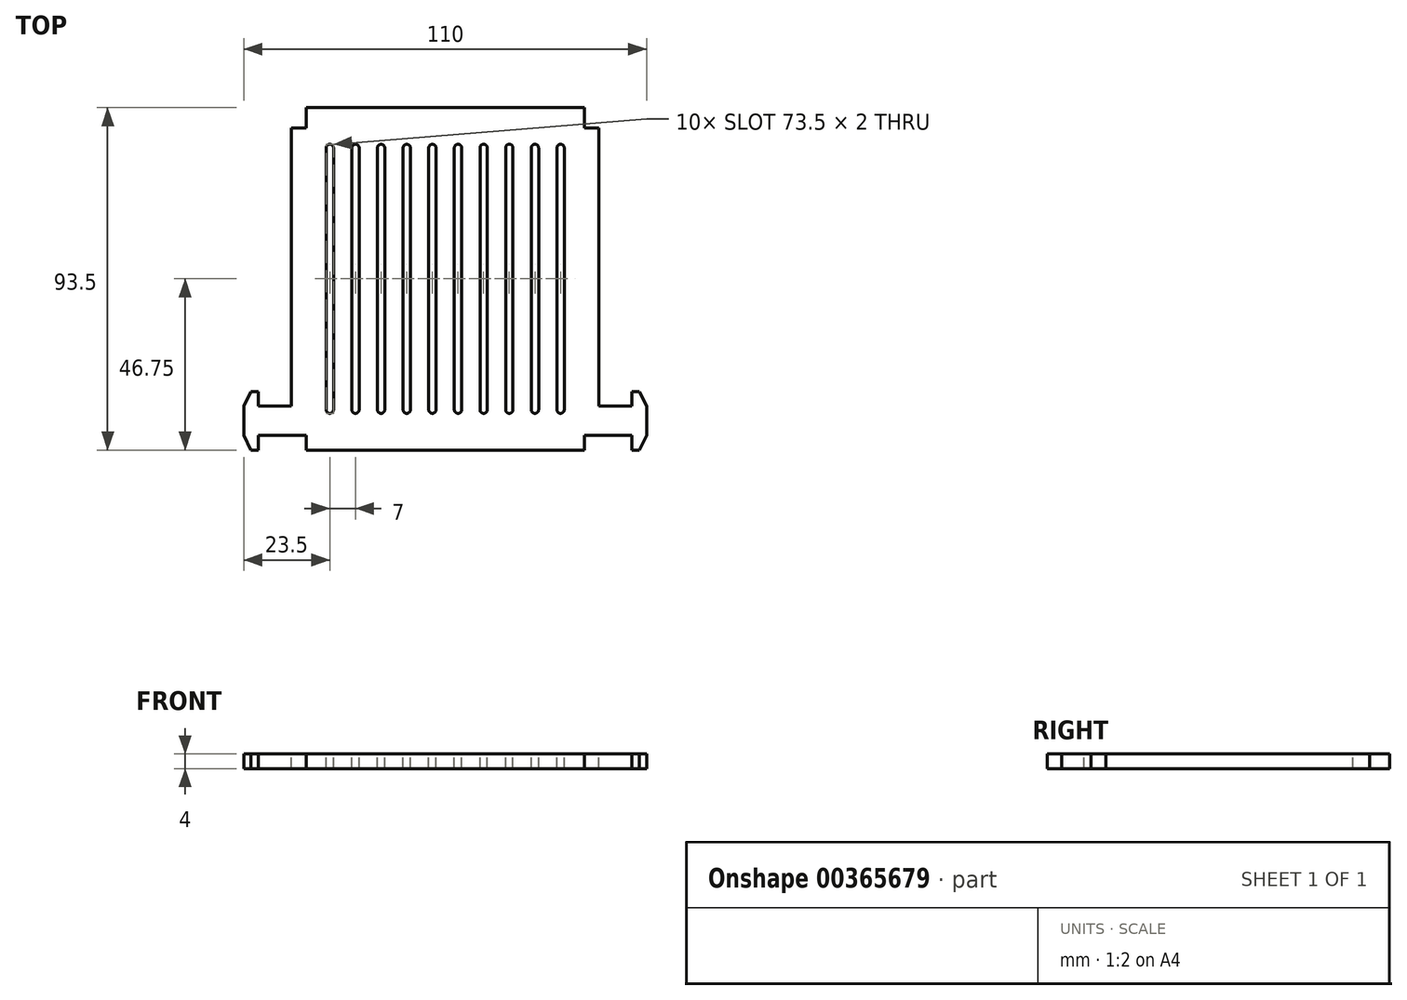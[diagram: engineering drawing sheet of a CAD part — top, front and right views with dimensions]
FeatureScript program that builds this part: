
annotation { "Feature Type Name" : "Feature", "Feature Type Description" : "" }
export const myFeature = defineFeature(function(context is Context, id is Id, definition is map)
    precondition{}
    {
        {
            var Q0;
            Q0=qCreatedBy(makeId("Top.planeOp"),FACE);
            var sketch = newSketch(context, id + "F0", { "sketchPlane" : qUnion([Q0])});
            skLineSegment(sketch, "E0.bottom", {"start": v(0, 0) * mm, "end": v(84, 0) * mm});
            skLineSegment(sketch, "E0.top", {"start": v(0, 93.5) * mm, "end": v(84, 93.5) * mm});
            skLineSegment(sketch, "E0.left", {"start": v(0, 0) * mm, "end": v(0, 93.5) * mm});
            skLineSegment(sketch, "E0.right", {"start": v(84, 0) * mm, "end": v(84, 93.5) * mm});
            skSolve(sketch);
        }
        {
            var Q0;
            Q0=qSketchRegion(id+"F0",true);
            extrude(context, id + "F1", {"entities" : qUnion([Q0]), "depth" : 4 * mm});
        }
        {
            var Q0;
            Q0=makeQuery(id+"F1.opExtrude","CAP_FACE",FACE,{"disambiguationData":[OSD([sQuery(id+"F0.wireOp",EDGE,"E0.bottom"),sQuery(id+"F0.wireOp",EDGE,"E0.top"),sQuery(id+"F0.wireOp",EDGE,"E0.left"),sQuery(id+"F0.wireOp",EDGE,"E0.right")])],"isStart":false});
            var sketch = newSketch(context, id + "F2", { "sketchPlane" : qUnion([Q0])});
            skLineSegment(sketch, "E1.bottom", {"start": v(0, 0) * mm, "end": v(4, 0) * mm});
            skLineSegment(sketch, "E1.top", {"start": v(0, 4) * mm, "end": v(4, 4) * mm});
            skLineSegment(sketch, "E1.left", {"start": v(0, 0) * mm, "end": v(0, 4) * mm});
            skLineSegment(sketch, "E1.right", {"start": v(4, 0) * mm, "end": v(4, 4) * mm});
            skLineSegment(sketch, "E2.1.0.0", {"start": v(80, 0) * mm, "end": v(84, 0) * mm});
            skLineSegment(sketch, "E2.1.0.1", {"start": v(80, 4) * mm, "end": v(84, 4) * mm});
            skLineSegment(sketch, "E2.1.0.2", {"start": v(80, 0) * mm, "end": v(80, 4) * mm});
            skLineSegment(sketch, "E2.1.0.3", {"start": v(84, 0) * mm, "end": v(84, 4) * mm});
            skLineSegment(sketch, "E2.direction1", {"start": v(0, 0) * mm, "end": v(80, 0) * mm, "construction": true});
            skLineSegment(sketch, "E2.direction2", {"start": v(0, 0) * mm, "end": v(0, 88) * mm, "construction": true});
            skLineSegment(sketch, "E3", {"start": v(0, 88) * mm, "end": v(84, 88) * mm, "construction": true});
            skLineSegment(sketch, "E4.bottom", {"start": v(0, 88) * mm, "end": v(4, 88) * mm});
            skLineSegment(sketch, "E4.top", {"start": v(0, 93.5) * mm, "end": v(4, 93.5) * mm});
            skLineSegment(sketch, "E4.left", {"start": v(0, 88) * mm, "end": v(0, 93.5) * mm});
            skLineSegment(sketch, "E4.right", {"start": v(4, 88) * mm, "end": v(4, 93.5) * mm});
            skLineSegment(sketch, "E5.bottom", {"start": v(84, 88) * mm, "end": v(80, 88) * mm});
            skLineSegment(sketch, "E5.top", {"start": v(84, 93.5) * mm, "end": v(80, 93.5) * mm});
            skLineSegment(sketch, "E5.left", {"start": v(84, 88) * mm, "end": v(84, 93.5) * mm});
            skLineSegment(sketch, "E5.right", {"start": v(80, 88) * mm, "end": v(80, 93.5) * mm});
            skSolve(sketch);
        }
        {
            var Q0;
            Q0=qSketchRegion(id+"F2",true);
            extrude(context, id + "F3", {"entities" : qUnion([Q0]), "operationType" : NewBodyOperationType.REMOVE, "endBound" : BoundingType.UP_TO_NEXT, "oppositeDirection" : true, "depth" : 25 * mm});
        }
        {
            var Q0;
            Q0=makeQuery(id+"F1.opExtrude","CAP_FACE",FACE,{"disambiguationData":[OSD([sQuery(id+"F0.wireOp",EDGE,"E0.bottom"),sQuery(id+"F0.wireOp",EDGE,"E0.top"),sQuery(id+"F0.wireOp",EDGE,"E0.left"),sQuery(id+"F0.wireOp",EDGE,"E0.right")])],"isStart":false});
            var sketch = newSketch(context, id + "F4", { "sketchPlane" : qUnion([Q0])});
            skLineSegment(sketch, "E6.bottom", {"start": v(10.5, 83.5) * mm, "end": v(10.5, 83.5) * mm});
            skLineSegment(sketch, "E6.top", {"start": v(10.5, 10) * mm, "end": v(10.5, 10) * mm});
            skLineSegment(sketch, "E6.left", {"start": v(9.5, 82.5) * mm, "end": v(9.5, 11) * mm});
            skLineSegment(sketch, "E6.right", {"start": v(11.5, 82.5) * mm, "end": v(11.5, 11) * mm});
            skPoint(sketch, "E7.visualSharp", {"position": v(9.5, 83.5) * mm});
            skArc(sketch, "E7.filletArc", {"start": v(10.5, 83.5) * mm, "mid": v(9.8, 83.2) * mm, "end": v(9.5, 82.5) * mm});
            skArc(sketch, "E8.filletArc", {"start": v(11.5, 82.5) * mm, "mid": v(11.2, 83.2) * mm, "end": v(10.5, 83.5) * mm});
            skPoint(sketch, "E9.visualSharp", {"position": v(11.5, 10) * mm});
            skArc(sketch, "E9.filletArc", {"start": v(10.5, 10) * mm, "mid": v(11.2, 10.3) * mm, "end": v(11.5, 11) * mm});
            skPoint(sketch, "E10.visualSharp", {"position": v(9.5, 10) * mm});
            skArc(sketch, "E10.filletArc", {"start": v(9.5, 11) * mm, "mid": v(9.8, 10.3) * mm, "end": v(10.5, 10) * mm});
            skPoint(sketch, "E11.1.0.0", {"position": v(16.5, 83.5) * mm});
            skLineSegment(sketch, "E11.1.0.1", {"start": v(16.5, 82.5) * mm, "end": v(16.5, 11) * mm});
            skLineSegment(sketch, "E11.1.0.2", {"start": v(18.5, 82.5) * mm, "end": v(18.5, 11) * mm});
            skPoint(sketch, "E11.1.0.3", {"position": v(18.5, 10) * mm});
            skPoint(sketch, "E11.1.0.4", {"position": v(16.5, 10) * mm});
            skArc(sketch, "E11.1.0.5", {"start": v(17.5, 10) * mm, "mid": v(18.2, 10.3) * mm, "end": v(18.5, 11) * mm});
            skArc(sketch, "E11.1.0.6", {"start": v(17.5, 83.5) * mm, "mid": v(16.8, 83.2) * mm, "end": v(16.5, 82.5) * mm});
            skArc(sketch, "E11.1.0.7", {"start": v(16.5, 11) * mm, "mid": v(16.8, 10.3) * mm, "end": v(17.5, 10) * mm});
            skArc(sketch, "E11.1.0.8", {"start": v(18.5, 82.5) * mm, "mid": v(18.2, 83.2) * mm, "end": v(17.5, 83.5) * mm});
            skPoint(sketch, "E11.2.0.0", {"position": v(23.5, 83.5) * mm});
            skLineSegment(sketch, "E11.2.0.1", {"start": v(23.5, 82.5) * mm, "end": v(23.5, 11) * mm});
            skLineSegment(sketch, "E11.2.0.2", {"start": v(25.5, 82.5) * mm, "end": v(25.5, 11) * mm});
            skPoint(sketch, "E11.2.0.3", {"position": v(25.5, 10) * mm});
            skPoint(sketch, "E11.2.0.4", {"position": v(23.5, 10) * mm});
            skArc(sketch, "E11.2.0.5", {"start": v(24.5, 10) * mm, "mid": v(25.2, 10.3) * mm, "end": v(25.5, 11) * mm});
            skArc(sketch, "E11.2.0.6", {"start": v(24.5, 83.5) * mm, "mid": v(23.8, 83.2) * mm, "end": v(23.5, 82.5) * mm});
            skArc(sketch, "E11.2.0.7", {"start": v(23.5, 11) * mm, "mid": v(23.8, 10.3) * mm, "end": v(24.5, 10) * mm});
            skArc(sketch, "E11.2.0.8", {"start": v(25.5, 82.5) * mm, "mid": v(25.2, 83.2) * mm, "end": v(24.5, 83.5) * mm});
            skPoint(sketch, "E11.3.0.0", {"position": v(30.5, 83.5) * mm});
            skLineSegment(sketch, "E11.3.0.1", {"start": v(30.5, 82.5) * mm, "end": v(30.5, 11) * mm});
            skLineSegment(sketch, "E11.3.0.2", {"start": v(32.5, 82.5) * mm, "end": v(32.5, 11) * mm});
            skPoint(sketch, "E11.3.0.3", {"position": v(32.5, 10) * mm});
            skPoint(sketch, "E11.3.0.4", {"position": v(30.5, 10) * mm});
            skArc(sketch, "E11.3.0.5", {"start": v(31.5, 10) * mm, "mid": v(32.2, 10.3) * mm, "end": v(32.5, 11) * mm});
            skArc(sketch, "E11.3.0.6", {"start": v(31.5, 83.5) * mm, "mid": v(30.8, 83.2) * mm, "end": v(30.5, 82.5) * mm});
            skArc(sketch, "E11.3.0.7", {"start": v(30.5, 11) * mm, "mid": v(30.8, 10.3) * mm, "end": v(31.5, 10) * mm});
            skArc(sketch, "E11.3.0.8", {"start": v(32.5, 82.5) * mm, "mid": v(32.2, 83.2) * mm, "end": v(31.5, 83.5) * mm});
            skPoint(sketch, "E11.4.0.0", {"position": v(37.5, 83.5) * mm});
            skLineSegment(sketch, "E11.4.0.1", {"start": v(37.5, 82.5) * mm, "end": v(37.5, 11) * mm});
            skLineSegment(sketch, "E11.4.0.2", {"start": v(39.5, 82.5) * mm, "end": v(39.5, 11) * mm});
            skPoint(sketch, "E11.4.0.3", {"position": v(39.5, 10) * mm});
            skPoint(sketch, "E11.4.0.4", {"position": v(37.5, 10) * mm});
            skArc(sketch, "E11.4.0.5", {"start": v(38.5, 10) * mm, "mid": v(39.2, 10.3) * mm, "end": v(39.5, 11) * mm});
            skArc(sketch, "E11.4.0.6", {"start": v(38.5, 83.5) * mm, "mid": v(37.8, 83.2) * mm, "end": v(37.5, 82.5) * mm});
            skArc(sketch, "E11.4.0.7", {"start": v(37.5, 11) * mm, "mid": v(37.8, 10.3) * mm, "end": v(38.5, 10) * mm});
            skArc(sketch, "E11.4.0.8", {"start": v(39.5, 82.5) * mm, "mid": v(39.2, 83.2) * mm, "end": v(38.5, 83.5) * mm});
            skPoint(sketch, "E11.5.0.0", {"position": v(44.5, 83.5) * mm});
            skLineSegment(sketch, "E11.5.0.1", {"start": v(44.5, 82.5) * mm, "end": v(44.5, 11) * mm});
            skLineSegment(sketch, "E11.5.0.2", {"start": v(46.5, 82.5) * mm, "end": v(46.5, 11) * mm});
            skPoint(sketch, "E11.5.0.3", {"position": v(46.5, 10) * mm});
            skPoint(sketch, "E11.5.0.4", {"position": v(44.5, 10) * mm});
            skArc(sketch, "E11.5.0.5", {"start": v(45.5, 10) * mm, "mid": v(46.2, 10.3) * mm, "end": v(46.5, 11) * mm});
            skArc(sketch, "E11.5.0.6", {"start": v(45.5, 83.5) * mm, "mid": v(44.8, 83.2) * mm, "end": v(44.5, 82.5) * mm});
            skArc(sketch, "E11.5.0.7", {"start": v(44.5, 11) * mm, "mid": v(44.8, 10.3) * mm, "end": v(45.5, 10) * mm});
            skArc(sketch, "E11.5.0.8", {"start": v(46.5, 82.5) * mm, "mid": v(46.2, 83.2) * mm, "end": v(45.5, 83.5) * mm});
            skPoint(sketch, "E11.6.0.0", {"position": v(51.5, 83.5) * mm});
            skLineSegment(sketch, "E11.6.0.1", {"start": v(51.5, 82.5) * mm, "end": v(51.5, 11) * mm});
            skLineSegment(sketch, "E11.6.0.2", {"start": v(53.5, 82.5) * mm, "end": v(53.5, 11) * mm});
            skPoint(sketch, "E11.6.0.3", {"position": v(53.5, 10) * mm});
            skPoint(sketch, "E11.6.0.4", {"position": v(51.5, 10) * mm});
            skArc(sketch, "E11.6.0.5", {"start": v(52.5, 10) * mm, "mid": v(53.2, 10.3) * mm, "end": v(53.5, 11) * mm});
            skArc(sketch, "E11.6.0.6", {"start": v(52.5, 83.5) * mm, "mid": v(51.8, 83.2) * mm, "end": v(51.5, 82.5) * mm});
            skArc(sketch, "E11.6.0.7", {"start": v(51.5, 11) * mm, "mid": v(51.8, 10.3) * mm, "end": v(52.5, 10) * mm});
            skArc(sketch, "E11.6.0.8", {"start": v(53.5, 82.5) * mm, "mid": v(53.2, 83.2) * mm, "end": v(52.5, 83.5) * mm});
            skPoint(sketch, "E11.7.0.0", {"position": v(58.5, 83.5) * mm});
            skLineSegment(sketch, "E11.7.0.1", {"start": v(58.5, 82.5) * mm, "end": v(58.5, 11) * mm});
            skLineSegment(sketch, "E11.7.0.2", {"start": v(60.5, 82.5) * mm, "end": v(60.5, 11) * mm});
            skPoint(sketch, "E11.7.0.3", {"position": v(60.5, 10) * mm});
            skPoint(sketch, "E11.7.0.4", {"position": v(58.5, 10) * mm});
            skArc(sketch, "E11.7.0.5", {"start": v(59.5, 10) * mm, "mid": v(60.2, 10.3) * mm, "end": v(60.5, 11) * mm});
            skArc(sketch, "E11.7.0.6", {"start": v(59.5, 83.5) * mm, "mid": v(58.8, 83.2) * mm, "end": v(58.5, 82.5) * mm});
            skArc(sketch, "E11.7.0.7", {"start": v(58.5, 11) * mm, "mid": v(58.8, 10.3) * mm, "end": v(59.5, 10) * mm});
            skArc(sketch, "E11.7.0.8", {"start": v(60.5, 82.5) * mm, "mid": v(60.2, 83.2) * mm, "end": v(59.5, 83.5) * mm});
            skPoint(sketch, "E11.8.0.0", {"position": v(65.5, 83.5) * mm});
            skLineSegment(sketch, "E11.8.0.1", {"start": v(65.5, 82.5) * mm, "end": v(65.5, 11) * mm});
            skLineSegment(sketch, "E11.8.0.2", {"start": v(67.5, 82.5) * mm, "end": v(67.5, 11) * mm});
            skPoint(sketch, "E11.8.0.3", {"position": v(67.5, 10) * mm});
            skPoint(sketch, "E11.8.0.4", {"position": v(65.5, 10) * mm});
            skArc(sketch, "E11.8.0.5", {"start": v(66.5, 10) * mm, "mid": v(67.2, 10.3) * mm, "end": v(67.5, 11) * mm});
            skArc(sketch, "E11.8.0.6", {"start": v(66.5, 83.5) * mm, "mid": v(65.8, 83.2) * mm, "end": v(65.5, 82.5) * mm});
            skArc(sketch, "E11.8.0.7", {"start": v(65.5, 11) * mm, "mid": v(65.8, 10.3) * mm, "end": v(66.5, 10) * mm});
            skArc(sketch, "E11.8.0.8", {"start": v(67.5, 82.5) * mm, "mid": v(67.2, 83.2) * mm, "end": v(66.5, 83.5) * mm});
            skPoint(sketch, "E11.9.0.0", {"position": v(72.5, 83.5) * mm});
            skLineSegment(sketch, "E11.9.0.1", {"start": v(72.5, 82.5) * mm, "end": v(72.5, 11) * mm});
            skLineSegment(sketch, "E11.9.0.2", {"start": v(74.5, 82.5) * mm, "end": v(74.5, 11) * mm});
            skPoint(sketch, "E11.9.0.3", {"position": v(74.5, 10) * mm});
            skPoint(sketch, "E11.9.0.4", {"position": v(72.5, 10) * mm});
            skArc(sketch, "E11.9.0.5", {"start": v(73.5, 10) * mm, "mid": v(74.2, 10.3) * mm, "end": v(74.5, 11) * mm});
            skArc(sketch, "E11.9.0.6", {"start": v(73.5, 83.5) * mm, "mid": v(72.8, 83.2) * mm, "end": v(72.5, 82.5) * mm});
            skArc(sketch, "E11.9.0.7", {"start": v(72.5, 11) * mm, "mid": v(72.8, 10.3) * mm, "end": v(73.5, 10) * mm});
            skArc(sketch, "E11.9.0.8", {"start": v(74.5, 82.5) * mm, "mid": v(74.2, 83.2) * mm, "end": v(73.5, 83.5) * mm});
            skLineSegment(sketch, "E11.direction1", {"start": v(9.5, 10) * mm, "end": v(16.5, 10) * mm, "construction": true});
            skSolve(sketch);
        }
        {
            var Q0;
            Q0=qSketchRegion(id+"F4",true);
            extrude(context, id + "F5", {"entities" : qUnion([Q0]), "operationType" : NewBodyOperationType.REMOVE, "endBound" : BoundingType.UP_TO_NEXT, "oppositeDirection" : true, "depth" : 25 * mm});
        }
        {
            var Q0;
            Q0=makeQuery(id+"F1.opExtrude","CAP_FACE",FACE,{"disambiguationData":[OSD([sQuery(id+"F0.wireOp",EDGE,"E0.bottom"),sQuery(id+"F0.wireOp",EDGE,"E0.top"),sQuery(id+"F0.wireOp",EDGE,"E0.left"),sQuery(id+"F0.wireOp",EDGE,"E0.right")])],"isStart":false});
            var sketch = newSketch(context, id + "F6", { "sketchPlane" : qUnion([Q0])});
            skLineSegment(sketch, "E12.bottom", {"start": v(84, 4) * mm, "end": v(97, 4) * mm});
            skLineSegment(sketch, "E12.top", {"start": v(84, 12) * mm, "end": v(97, 12) * mm});
            skLineSegment(sketch, "E12.left", {"start": v(84, 4) * mm, "end": v(84, 12) * mm});
            skLineSegment(sketch, "E12.right", {"start": v(97, 4) * mm, "end": v(97, 12) * mm});
            skLineSegment(sketch, "E13", {"start": v(42, 0) * mm, "end": v(42, 93.5) * mm, "construction": true});
            skLineSegment(sketch, "E14.MirrorCS", {"start": v(-13, 4) * mm, "end": v(-13, 12) * mm});
            skLineSegment(sketch, "E15.MirrorCS", {"start": v(0, 4) * mm, "end": v(0, 12) * mm});
            skLineSegment(sketch, "E16.MirrorCS", {"start": v(0, 12) * mm, "end": v(-13, 12) * mm});
            skLineSegment(sketch, "E17.MirrorCS", {"start": v(0, 4) * mm, "end": v(-13, 4) * mm});
            skSolve(sketch);
        }
        {
            var Q0;
            Q0 = qSketchRegion(id + "F6", true);
            extrude(context, id + "F7", {"entities" : qUnion([Q0]), "operationType" : NewBodyOperationType.ADD, "oppositeDirection" : true, "depth" : 4 * mm});
        }
        {
            var Q0;
            Q0=makeQuery(id+"F7.boolean.opBoolean","MERGE",FACE,{"derivedFrom":[makeQuery(id+"F1.opExtrude","CAP_FACE",FACE,{"disambiguationData":[OSD([sQuery(id+"F0.wireOp",EDGE,"E0.bottom"),sQuery(id+"F0.wireOp",EDGE,"E0.top"),sQuery(id+"F0.wireOp",EDGE,"E0.left"),sQuery(id+"F0.wireOp",EDGE,"E0.right")])],"isStart":false}),makeQuery(id+"F7.opExtrude","CAP_FACE",FACE,{"disambiguationData":[OSD([sQuery(id+"F6.wireOp",EDGE,"E12.bottom"),sQuery(id+"F6.wireOp",EDGE,"E12.top"),sQuery(id+"F6.wireOp",EDGE,"E12.left"),sQuery(id+"F6.wireOp",EDGE,"E12.right")])],"isStart":true}),makeQuery(id+"F7.opExtrude","CAP_FACE",FACE,{"disambiguationData":[OSD([sQuery(id+"F6.wireOp",EDGE,"E14.MirrorCS"),sQuery(id+"F6.wireOp",EDGE,"E15.MirrorCS"),sQuery(id+"F6.wireOp",EDGE,"E16.MirrorCS"),sQuery(id+"F6.wireOp",EDGE,"E17.MirrorCS")])],"isStart":true})]});
            var sketch = newSketch(context, id + "F8", { "sketchPlane" : qUnion([Q0])});
            skLineSegment(sketch, "E18", {"start": v(93, 12) * mm, "end": v(93, 16) * mm});
            skLineSegment(sketch, "E19", {"start": v(93, 16) * mm, "end": v(95, 16) * mm});
            skLineSegment(sketch, "E20", {"start": v(95, 16) * mm, "end": v(97, 12) * mm});
            skLineSegment(sketch, "E21", {"start": v(97, 12) * mm, "end": v(93, 12) * mm});
            skLineSegment(sketch, "E22", {"start": v(97, 8) * mm, "end": v(-13, 8) * mm, "construction": true});
            skLineSegment(sketch, "E23.MirrorCS", {"start": v(93, 0) * mm, "end": v(95, 0) * mm});
            skLineSegment(sketch, "E24.MirrorCS", {"start": v(95, 0) * mm, "end": v(97, 4) * mm});
            skLineSegment(sketch, "E25.MirrorCS", {"start": v(93, 4) * mm, "end": v(93, 0) * mm});
            skLineSegment(sketch, "E26.MirrorCS", {"start": v(97, 4) * mm, "end": v(93, 4) * mm});
            skPoint(sketch, "E27.endSnap0", {"position": v(60.5, 46.75) * mm});
            skLineSegment(sketch, "E28", {"start": v(42, 0) * mm, "end": v(42, 93.5) * mm, "construction": true});
            skLineSegment(sketch, "E29.MirrorCS", {"start": v(-13, 12) * mm, "end": v(-9, 12) * mm});
            skLineSegment(sketch, "E30.MirrorCS", {"start": v(-9, 12) * mm, "end": v(-9, 16) * mm});
            skLineSegment(sketch, "E31.MirrorCS", {"start": v(-9, 16) * mm, "end": v(-11, 16) * mm});
            skLineSegment(sketch, "E32.MirrorCS", {"start": v(-11, 16) * mm, "end": v(-13, 12) * mm});
            skLineSegment(sketch, "E33.MirrorCS", {"start": v(-9, 0) * mm, "end": v(-11, 0) * mm});
            skLineSegment(sketch, "E34.MirrorCS", {"start": v(-11, 0) * mm, "end": v(-13, 4) * mm});
            skLineSegment(sketch, "E35.MirrorCS", {"start": v(-9, 4) * mm, "end": v(-9, 0) * mm});
            skLineSegment(sketch, "E36.MirrorCS", {"start": v(-13, 4) * mm, "end": v(-9, 4) * mm});
            skSolve(sketch);
        }
        {
            var Q0;
            Q0 = qSketchRegion(id + "F8", true);
            extrude(context, id + "F9", {"entities" : qUnion([Q0]), "operationType" : NewBodyOperationType.ADD, "oppositeDirection" : true, "depth" : 4 * mm});
        }
    });
